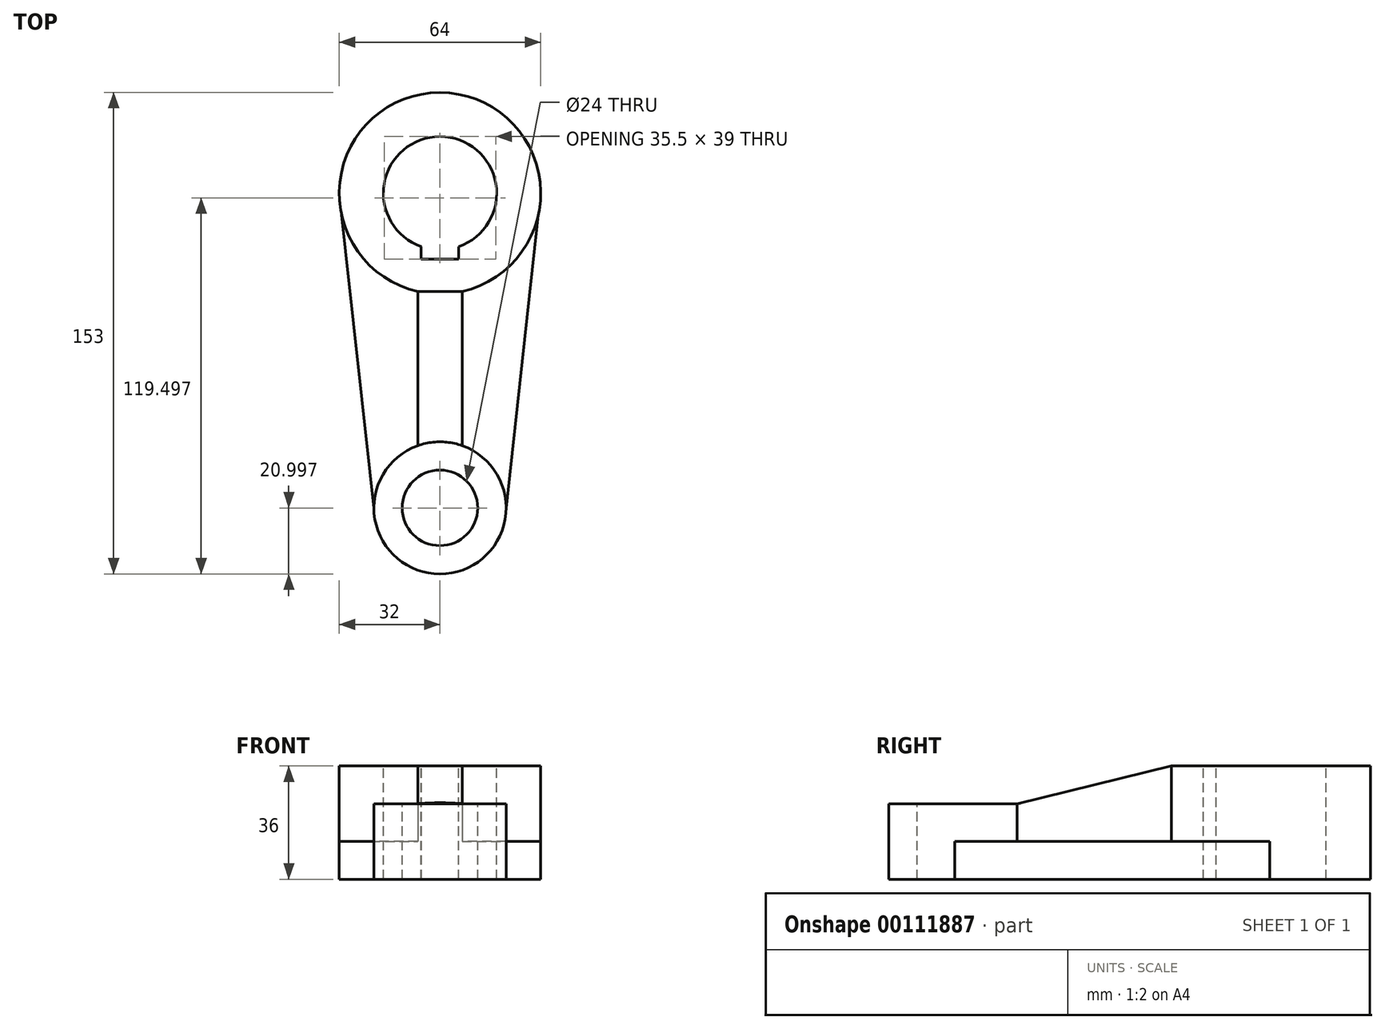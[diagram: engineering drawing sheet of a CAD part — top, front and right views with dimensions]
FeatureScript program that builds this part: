
annotation { "Feature Type Name" : "Feature", "Feature Type Description" : "" }
export const myFeature = defineFeature(function(context is Context, id is Id, definition is map)
    precondition{}
    {
        {
            var Q0;
            Q0=qCreatedBy(makeId("Top.planeOp"),FACE);
            var sketch = newSketch(context, id + "F0", { "sketchPlane" : qUnion([Q0])});
            skCircle(sketch, "E0", {"center": v(0, -51.81) * mm, "radius": 21 * mm});
            skCircle(sketch, "E1", {"center": v(0, 48.19) * mm, "radius": 32 * mm});
            skPoint(sketch, "E2", {"position": v(-32, 48.19) * mm});
            skPoint(sketch, "E3", {"position": v(32, 48.19) * mm});
            skPoint(sketch, "E4", {"position": v(21, -51.81) * mm});
            skPoint(sketch, "E5", {"position": v(-21, -51.81) * mm});
            skLineSegment(sketch, "E6", {"start": v(-32, 48.19) * mm, "end": v(-21, -51.81) * mm});
            skLineSegment(sketch, "E7", {"start": v(32, 48.19) * mm, "end": v(21, -51.81) * mm});
            skCircle(sketch, "E8", {"center": v(0, -51.81) * mm, "radius": 9.48 * mm});
            skCircle(sketch, "E9", {"center": v(0, 48.19) * mm, "radius": 18 * mm});
            skPoint(sketch, "E10", {"position": v(0, 30.19) * mm});
            skLineSegment(sketch, "E11.bottom", {"start": v(-6, 28.19) * mm, "end": v(6, 28.19) * mm});
            skLineSegment(sketch, "E11.left", {"start": v(-6, 28.19) * mm, "end": v(-6, 31.22) * mm});
            skLineSegment(sketch, "E11.right", {"start": v(6, 28.19) * mm, "end": v(6, 31.22) * mm});
            skPoint(sketch, "E12.orphan", {"position": v(6, 32.19) * mm});
            skPoint(sketch, "E13.orphan", {"position": v(-6, 32.19) * mm});
            skSolve(sketch);
        }
        {
            var Q0;
            {var subQ0=sQuery(id+"F0.wireOp",EDGE,"E6");var subQ1=sQuery(id+"F0.wireOp",EDGE,"E1");var subQ2=makeQuery(id+"F0.imprint","INTERSECT",VERTEX,{"disambiguationData":[OD(0.0)],"derivedFrom":[subQ1,subQ0]});Q0=makeQuery(id+"F0.imprint","IMPRINT",FACE,{"disambiguationData":[TD([[makeQuery(id+"F0.imprint","IMPRINT",EDGE,{"disambiguationData":[TD([[subQ2,-1.0]])],"derivedFrom":subQ1}),1.0]])]});}
            var Q1;
            {var subQ0=sQuery(id+"F0.wireOp",EDGE,"E7");var subQ1=sQuery(id+"F0.wireOp",EDGE,"E1");var subQ2=makeQuery(id+"F0.imprint","INTERSECT",VERTEX,{"disambiguationData":[OD(0.0)],"derivedFrom":[subQ1,subQ0]});Q1=makeQuery(id+"F0.imprint","IMPRINT",FACE,{"disambiguationData":[TD([[makeQuery(id+"F0.imprint","IMPRINT",EDGE,{"disambiguationData":[TD([[subQ2,1.0]])],"derivedFrom":subQ1}),1.0]])]});}
            var Q2;
            Q2=makeQuery(id+"F0.imprint","IMPRINT",FACE,{"disambiguationData":[TD([[makeQuery(id+"F0.imprint","IMPRINT",EDGE,{"derivedFrom":sQuery(id+"F0.wireOp",EDGE,"E8")}),-1.0]])]});
            var Q3;
            {var subQ0=sQuery(id+"F0.wireOp",EDGE,"E6");var subQ1=sQuery(id+"F0.wireOp",EDGE,"E0");var subQ2=makeQuery(id+"F0.imprint","INTERSECT",VERTEX,{"derivedFrom":[subQ1,subQ0]});Q3=makeQuery(id+"F0.imprint","IMPRINT",FACE,{"disambiguationData":[TD([[makeQuery(id+"F0.imprint","IMPRINT",EDGE,{"disambiguationData":[TD([[subQ2,1.0]])],"derivedFrom":subQ1}),-1.0]])]});}
            var Q4;
            Q4=makeQuery(id+"F0.imprint","IMPRINT",FACE,{"disambiguationData":[TD([[makeQuery(id+"F0.imprint","IMPRINT",EDGE,{"derivedFrom":sQuery(id+"F0.wireOp",EDGE,"E8")}),1.0]])]});
            var Q5;
            {var subQ0=sQuery(id+"F0.wireOp",EDGE,"E9");var subQ1=makeQuery(id+"F0.imprint","INTERSECT",VERTEX,{"derivedFrom":[subQ0,sQuery(id+"F0.wireOp",EDGE,"E11.left")]});Q5=makeQuery(id+"F0.imprint","IMPRINT",FACE,{"disambiguationData":[TD([[makeQuery(id+"F0.imprint","IMPRINT",EDGE,{"disambiguationData":[TD([[subQ1,-1.0]])],"derivedFrom":subQ0}),1.0]])]});}
            var Q6;
            Q6=makeQuery(id+"F0.imprint","IMPRINT",FACE,{"disambiguationData":[TD([[makeQuery(id+"F0.imprint","IMPRINT",EDGE,{"derivedFrom":sQuery(id+"F0.wireOp",EDGE,"E11.bottom")}),1.0]])]});
            var Q7;
            Q7=makeQuery(id+"F0.imprint","IMPRINT",FACE,{"disambiguationData":[TD([[makeQuery(id+"F0.imprint","IMPRINT",EDGE,{"derivedFrom":sQuery(id+"F0.wireOp",EDGE,"E11.bottom")}),-1.0]])]});
            extrude(context, id + "F1", {"entities" : qUnion([Q0, Q1, Q2, Q3, Q4, Q5, Q6, Q7]), "depth" : 12 * mm});
        }
        {
            var Q0;
            Q0=makeQuery(id+"F1.opExtrude","CAP_FACE",FACE,{"disambiguationData":[OSD([sQuery(id+"F0.wireOp",EDGE,"E0"),sQuery(id+"F0.wireOp",EDGE,"E1"),sQuery(id+"F0.wireOp",EDGE,"E6"),sQuery(id+"F0.wireOp",EDGE,"E7")])],"isStart":false});
            var sketch = newSketch(context, id + "F2", { "sketchPlane" : qUnion([Q0])});
            skPoint(sketch, "E14", {"position": v(0, 48.19) * mm});
            skCircle(sketch, "E15", {"center": v(0, 48.19) * mm, "radius": 32 * mm});
            skSolve(sketch);
        }
        {
            var Q0;
            Q0 = qSketchRegion(id + "F2", true);
            extrude(context, id + "F3", {"entities" : qUnion([Q0]), "operationType" : NewBodyOperationType.ADD, "depth" : 24 * mm});
        }
        {
            var Q0;
            Q0=makeQuery(id+"F1.opExtrude","CAP_FACE",FACE,{"disambiguationData":[OSD([sQuery(id+"F0.wireOp",EDGE,"E0"),sQuery(id+"F0.wireOp",EDGE,"E1"),sQuery(id+"F0.wireOp",EDGE,"E6"),sQuery(id+"F0.wireOp",EDGE,"E7")])],"isStart":false});
            var sketch = newSketch(context, id + "F4", { "sketchPlane" : qUnion([Q0])});
            skPoint(sketch, "E16", {"position": v(0, -51.81) * mm});
            skCircle(sketch, "E17", {"center": v(0, -51.81) * mm, "radius": 21 * mm});
            skSolve(sketch);
        }
        {
            var Q0;
            Q0 = qSketchRegion(id + "F4", true);
            extrude(context, id + "F5", {"entities" : qUnion([Q0]), "operationType" : NewBodyOperationType.ADD, "depth" : 12 * mm});
        }
        {
            var Q0;
            Q0=makeQuery(id+"F3.opExtrude","CAP_FACE",FACE,{"disambiguationData":[OSD([sQuery(id+"F2.wireOp",EDGE,"E15")])],"isStart":false});
            var sketch = newSketch(context, id + "F6", { "sketchPlane" : qUnion([Q0])});
            skPoint(sketch, "E18", {"position": v(0, 48.19) * mm});
            skArc(sketch, "E19", {"start": v(5.92, 31.19) * mm, "mid": v(0, 66.19) * mm, "end": v(-5.92, 31.19) * mm});
            skLineSegment(sketch, "E20.bottom", {"start": v(6, 27.19) * mm, "end": v(-6, 27.19) * mm});
            skLineSegment(sketch, "E20.top", {"start": v(6, 31.19) * mm, "end": v(5.92, 31.19) * mm});
            skLineSegment(sketch, "E20.left", {"start": v(6, 27.19) * mm, "end": v(6, 31.19) * mm});
            skLineSegment(sketch, "E20.right", {"start": v(-6, 27.19) * mm, "end": v(-6, 31.19) * mm});
            skPoint(sketch, "E21", {"position": v(0, 31.19) * mm});
            skLineSegment(sketch, "E22", {"start": v(0, 31.19) * mm, "end": v(0, 48.19) * mm});
            skLineSegment(sketch, "E23.trimOffspring", {"start": v(-5.92, 31.19) * mm, "end": v(-6, 31.19) * mm});
            skSolve(sketch);
        }
        {
            var Q0;
            Q0 = qSketchRegion(id + "F6", true);
            extrude(context, id + "F7", {"entities" : qUnion([Q0]), "operationType" : NewBodyOperationType.REMOVE, "endBound" : BoundingType.THROUGH_ALL, "oppositeDirection" : true, "depth" : 25 * mm});
        }
        {
            var Q0;
            Q0=makeQuery(id+"F5.opExtrude","CAP_FACE",FACE,{"disambiguationData":[OSD([sQuery(id+"F4.wireOp",EDGE,"E17")])],"isStart":false});
            var sketch = newSketch(context, id + "F8", { "sketchPlane" : qUnion([Q0])});
            skPoint(sketch, "E24", {"position": v(0, -51.81) * mm});
            skCircle(sketch, "E25", {"center": v(0, -51.81) * mm, "radius": 12 * mm});
            skSolve(sketch);
        }
        {
            var Q0;
            Q0 = qSketchRegion(id + "F8", true);
            extrude(context, id + "F9", {"entities" : qUnion([Q0]), "operationType" : NewBodyOperationType.REMOVE, "endBound" : BoundingType.THROUGH_ALL, "oppositeDirection" : true, "depth" : 25 * mm});
        }
        {
            var Q0;
            Q0=makeQuery(id+"F1.opExtrude","CAP_FACE",FACE,{"disambiguationData":[OSD([sQuery(id+"F0.wireOp",EDGE,"E0"),sQuery(id+"F0.wireOp",EDGE,"E1"),sQuery(id+"F0.wireOp",EDGE,"E6"),sQuery(id+"F0.wireOp",EDGE,"E7")])],"isStart":false});
            var sketch = newSketch(context, id + "F10", { "sketchPlane" : qUnion([Q0])});
            skCircle(sketch, "E26.0", {"center": v(0, -51.81) * mm, "radius": 21 * mm});
            skCircle(sketch, "E27.0", {"center": v(0, 48.19) * mm, "radius": 32 * mm});
            skLineSegment(sketch, "E28", {"start": v(-7.04, -32.03) * mm, "end": v(-7.04, 16.97) * mm});
            skLineSegment(sketch, "E29", {"start": v(7.04, -32.03) * mm, "end": v(7.04, 16.97) * mm});
            skSolve(sketch);
        }
        {
            var Q0;
            {var subQ0=sQuery(id+"F10.wireOp",EDGE,"E28");Q0=makeQuery(id+"F10.imprint","IMPRINT",FACE,{"disambiguationData":[TD([[makeQuery(id+"F10.imprint","IMPRINT",EDGE,{"derivedFrom":subQ0}),-1.0]])]});}
            extrude(context, id + "F11", {"entities" : qUnion([Q0]), "operationType" : NewBodyOperationType.ADD, "depth" : 24 * mm});
        }
        {
            var Q0;
            Q0=makeQuery(id+"F11.opExtrude","SWEPT_FACE",FACE,{"disambiguationData":[OSD([sQuery(id+"F10.wireOp",EDGE,"E29")])]});
            var sketch = newSketch(context, id + "F12", { "sketchPlane" : qUnion([Q0])});
            skLineSegment(sketch, "E30", {"start": v(-32.03, 24) * mm, "end": v(16.97, 36) * mm});
            skLineSegment(sketch, "E31", {"start": v(16.97, 36) * mm, "end": v(-32.03, 36) * mm});
            skLineSegment(sketch, "E32", {"start": v(-32.03, 36) * mm, "end": v(-32.03, 24) * mm});
            skSolve(sketch);
        }
        {
            var Q0;
            Q0=makeQuery(id+"F12.imprint","IMPRINT",FACE,{"disambiguationData":[TD([[makeQuery(id+"F12.imprint","IMPRINT",EDGE,{"derivedFrom":sQuery(id+"F12.wireOp",EDGE,"E30")}),1.0]])]});
            extrude(context, id + "F13", {"entities" : qUnion([Q0]), "operationType" : NewBodyOperationType.REMOVE, "oppositeDirection" : true, "depth" : 25 * mm});
        }
    });
